# Revit family: Door-Exterior-Simpson-Nantucket-Full_Panel-Single
name_source: partatom
category: Doors
revit_build: Autodesk Revit Architecture 2012 (Build: 20110916_2132(x64)
units: mm (PartAtom-declared; Revit-internal decimal feet)

## types (84) — shared parameters
Assembly Code = B2030230
Bottom Panel Height = 2' - 0 1/8"
Bottom Rail Height = 0' - 8 11/16"
Construction Type = Wood
Description = Nantucket Exterior Door
Frame = Wood - Simpson Doors - Douglas Fir
Frame Projection Ext. = 0' - 1"
Frame Projection Int. = 0' - 1"
Frame Type = Frame : Standard
Frame Width = 0' - 3"
Function = Exterior
Glass Options = http://simpsondoor.com
Innerbond Double Hip-Raised Panel = No
Innerbond Double Hip-Raised Panel Top = No
Manufacturer = Simpsons Door Company
Middle Rail Height 1 = 0' - 3 1/2"
Middle Rail Height 2 = 0' - 6 1/2"
Muntin Width = 0' - 0 3/8"
Number of Panel Dividers = 1
Ovolo Construction = Yes
Panel = Wood - Simpson Doors - Douglas Fir
Panel Divider Width = 0' - 3 1/2"
Panel Stile Width = 0' - 5"
Product Documentation Link = http://www.simpsondoor.com
Product Page URL = http://www.simpsondoor.com
Thickness = 0' - 1 3/4"
Thickness Note = comes in 1 3/4" and 2 1/4" Thickness. Default is set to 1 3/4"
Top Rail Height = 0' - 4 15/16"
URL = http://www.simpsondoor.com
Wall Closure = By host
Wood Species = http://simpsondoor.com

## per-type parameters (varying)
| type | Height | Model | Rough Height | Rough Width | Top Panel | Top Panel Height | Upper Mid Rail | Width |
| 77130 Nantucket 30x80 Ovolo Flat Panel | 6' - 8" | 77130 | 6' - 10" | 2' - 10" | Wood - Simpson Doors - Douglas Fir | 0' - 8 1/8" | Yes | 2' - 6" |
| 77130 Nantucket 30x84 Ovolo Flat Panel | 7' - 0" | 77130 | 7' - 2" | 2' - 10" | Wood - Simpson Doors - Douglas Fir | 0' - 8 1/8" | Yes | 2' - 6" |
| 77130 Nantucket 30x96 Ovolo Flat Panel | 8' - 0" | 77130 | 8' - 2" | 2' - 10" | Wood - Simpson Doors - Douglas Fir | 0' - 8 1/8" | Yes | 2' - 6" |
| 77130 Nantucket 32x80 Ovolo Flat Panel | 6' - 8" | 77130 | 6' - 10" | 3' - 0" | Wood - Simpson Doors - Douglas Fir | 0' - 8 1/8" | Yes | 2' - 8" |
| 77130 Nantucket 32x84 Ovolo Flat Panel | 7' - 0" | 77130 | 7' - 2" | 3' - 0" | Wood - Simpson Doors - Douglas Fir | 0' - 8 1/8" | Yes | 2' - 8" |
| 77130 Nantucket 32x96 Ovolo Flat Panel | 8' - 0" | 77130 | 8' - 2" | 3' - 0" | Wood - Simpson Doors - Douglas Fir | 0' - 8 1/8" | Yes | 2' - 8" |
| 77130 Nantucket 34x80 Ovolo Flat Panel | 6' - 8" | 77130 | 6' - 10" | 3' - 2" | Wood - Simpson Doors - Douglas Fir | 0' - 8 1/8" | Yes | 2' - 10" |
| 77130 Nantucket 34x84 Ovolo Flat Panel | 7' - 0" | 77130 | 7' - 2" | 3' - 2" | Wood - Simpson Doors - Douglas Fir | 0' - 8 1/8" | Yes | 2' - 10" |
| 77130 Nantucket 34x96 Ovolo Flat Panel | 8' - 0" | 77130 | 8' - 2" | 3' - 2" | Wood - Simpson Doors - Douglas Fir | 0' - 8 1/8" | Yes | 2' - 10" |
| 77130 Nantucket 36x80 Ovolo Flat Panel | 6' - 8" | 77130 | 6' - 10" | 3' - 4" | Wood - Simpson Doors - Douglas Fir | 0' - 8 1/8" | Yes | 3' - 0" |
| 77130 Nantucket 36x84 Ovolo Flat Panel | 7' - 0" | 77130 | 7' - 2" | 3' - 4" | Wood - Simpson Doors - Douglas Fir | 0' - 8 1/8" | Yes | 3' - 0" |
| 77130 Nantucket 36x96 Ovolo Flat Panel | 8' - 0" | 77130 | 8' - 2" | 3' - 4" | Wood - Simpson Doors - Douglas Fir | 0' - 8 1/8" | Yes | 3' - 0" |
| 77130 Nantucket 38x80 Ovolo Flat Panel | 6' - 8" | 77130 | 6' - 10" | 3' - 6" | Wood - Simpson Doors - Douglas Fir | 0' - 8 1/8" | Yes | 3' - 2" |
| 77130 Nantucket 38x84 Ovolo Flat Panel | 7' - 0" | 77130 | 7' - 2" | 3' - 6" | Wood - Simpson Doors - Douglas Fir | 0' - 8 1/8" | Yes | 3' - 2" |
| 77130 Nantucket 38x96 Ovolo Flat Panel | 8' - 0" | 77130 | 8' - 2" | 3' - 6" | Wood - Simpson Doors - Douglas Fir | 0' - 8 1/8" | Yes | 3' - 2" |
| 77130 Nantucket 40x80 Ovolo Flat Panel | 6' - 8" | 77130 | 6' - 10" | 3' - 8" | Wood - Simpson Doors - Douglas Fir | 0' - 8 1/8" | Yes | 3' - 4" |
| 77130 Nantucket 40x84 Ovolo Flat Panel | 7' - 0" | 77130 | 7' - 2" | 3' - 8" | Wood - Simpson Doors - Douglas Fir | 0' - 8 1/8" | Yes | 3' - 4" |
| 77130 Nantucket 40x96 Ovolo Flat Panel | 8' - 0" | 77130 | 8' - 2" | 3' - 8" | Wood - Simpson Doors - Douglas Fir | 0' - 8 1/8" | Yes | 3' - 4" |
| 77130 Nantucket 42x80 Ovolo Flat Panel | 6' - 8" | 77130 | 6' - 10" | 3' - 10" | Wood - Simpson Doors - Douglas Fir | 0' - 8 1/8" | Yes | 3' - 6" |
| 77130 Nantucket 42x84 Ovolo Flat Panel | 7' - 0" | 77130 | 7' - 2" | 3' - 10" | Wood - Simpson Doors - Douglas Fir | 0' - 8 1/8" | Yes | 3' - 6" |
| 77130 Nantucket 42x96 Ovolo Flat Panel | 8' - 0" | 77130 | 8' - 2" | 3' - 10" | Wood - Simpson Doors - Douglas Fir | 0' - 8 1/8" | Yes | 3' - 6" |
| 77132 Nantucket 30x80 Ovolo Flat Panel | 6' - 8" | 77132 | 6' - 10" | 2' - 10" | Glass - Simpson Doors - Clear | 0' - 8 1/8" | Yes | 2' - 6" |
| 77132 Nantucket 30x84 Ovolo Flat Panel | 7' - 0" | 77132 | 7' - 2" | 2' - 10" | Glass - Simpson Doors - Clear | 0' - 8 1/8" | Yes | 2' - 6" |
| 77132 Nantucket 30x96 Ovolo Flat Panel | 8' - 0" | 77132 | 8' - 2" | 2' - 10" | Glass - Simpson Doors - Clear | 0' - 8 1/8" | Yes | 2' - 6" |
| 77132 Nantucket 32x80 Ovolo Flat Panel | 6' - 8" | 77132 | 6' - 10" | 3' - 0" | Glass - Simpson Doors - Clear | 0' - 8 1/8" | Yes | 2' - 8" |
| 77132 Nantucket 32x84 Ovolo Flat Panel | 7' - 0" | 77132 | 7' - 2" | 3' - 0" | Glass - Simpson Doors - Clear | 0' - 8 1/8" | Yes | 2' - 8" |
| 77132 Nantucket 32x96 Ovolo Flat Panel | 8' - 0" | 77132 | 8' - 2" | 3' - 0" | Glass - Simpson Doors - Clear | 0' - 8 1/8" | Yes | 2' - 8" |
| 77132 Nantucket 34x80 Ovolo Flat Panel | 6' - 8" | 77132 | 6' - 10" | 3' - 2" | Glass - Simpson Doors - Clear | 0' - 8 1/8" | Yes | 2' - 10" |
| 77132 Nantucket 34x84 Ovolo Flat Panel | 7' - 0" | 77132 | 7' - 2" | 3' - 2" | Glass - Simpson Doors - Clear | 0' - 8 1/8" | Yes | 2' - 10" |
| 77132 Nantucket 34x96 Ovolo Flat Panel | 8' - 0" | 77132 | 8' - 2" | 3' - 2" | Glass - Simpson Doors - Clear | 0' - 8 1/8" | Yes | 2' - 10" |
| 77132 Nantucket 36x80 Ovolo Flat Panel | 6' - 8" | 77132 | 6' - 10" | 3' - 4" | Glass - Simpson Doors - Clear | 0' - 8 1/8" | Yes | 3' - 0" |
| 77132 Nantucket 36x84 Ovolo Flat Panel | 7' - 0" | 77132 | 7' - 2" | 3' - 4" | Glass - Simpson Doors - Clear | 0' - 8 1/8" | Yes | 3' - 0" |
| 77132 Nantucket 36x96 Ovolo Flat Panel | 8' - 0" | 77132 | 8' - 2" | 3' - 4" | Glass - Simpson Doors - Clear | 0' - 8 1/8" | Yes | 3' - 0" |
| 77132 Nantucket 38x80 Ovolo Flat Panel | 6' - 8" | 77132 | 6' - 10" | 3' - 6" | Glass - Simpson Doors - Clear | 0' - 8 1/8" | Yes | 3' - 2" |
| 77132 Nantucket 38x84 Ovolo Flat Panel | 7' - 0" | 77132 | 7' - 2" | 3' - 6" | Glass - Simpson Doors - Clear | 0' - 8 1/8" | Yes | 3' - 2" |
| 77132 Nantucket 38x96 Ovolo Flat Panel | 8' - 0" | 77132 | 8' - 2" | 3' - 6" | Glass - Simpson Doors - Clear | 0' - 8 1/8" | Yes | 3' - 2" |
| 77132 Nantucket 40x80 Ovolo Flat Panel | 6' - 8" | 77132 | 6' - 10" | 3' - 8" | Glass - Simpson Doors - Clear | 0' - 8 1/8" | Yes | 3' - 4" |
| 77132 Nantucket 40x84 Ovolo Flat Panel | 7' - 0" | 77132 | 7' - 2" | 3' - 8" | Glass - Simpson Doors - Clear | 0' - 8 1/8" | Yes | 3' - 4" |
| 77132 Nantucket 40x96 Ovolo Flat Panel | 8' - 0" | 77132 | 8' - 2" | 3' - 8" | Glass - Simpson Doors - Clear | 0' - 8 1/8" | Yes | 3' - 4" |
| 77132 Nantucket 42x80 Ovolo Flat Panel | 6' - 8" | 77132 | 6' - 10" | 3' - 10" | Glass - Simpson Doors - Clear | 0' - 8 1/8" | Yes | 3' - 6" |
| 77132 Nantucket 42x84 Ovolo Flat Panel | 7' - 0" | 77132 | 7' - 2" | 3' - 10" | Glass - Simpson Doors - Clear | 0' - 8 1/8" | Yes | 3' - 6" |
| 77132 Nantucket 42x96 Ovolo Flat Panel | 8' - 0" | 77132 | 8' - 2" | 3' - 10" | Glass - Simpson Doors - Clear | 0' - 8 1/8" | Yes | 3' - 6" |
| 77144 Nantucket 30x80 Ovolo Flat Panel | 6' - 8" | 77144 | 6' - 10" | 2' - 10" | Wood - Simpson Doors - Douglas Fir | 0' - 8 1/8" | No | 2' - 6" |
| 77144 Nantucket 30x84 Ovolo Flat Panel | 7' - 0" | 77144 | 7' - 2" | 2' - 10" | Wood - Simpson Doors - Douglas Fir | 0' - 8 1/8" | No | 2' - 6" |
| 77144 Nantucket 30x96 Ovolo Flat Panel | 8' - 0" | 77144 | 8' - 2" | 2' - 10" | Wood - Simpson Doors - Douglas Fir | 0' - 8 1/8" | No | 2' - 6" |
| 77144 Nantucket 32x80 Ovolo Flat Panel | 6' - 8" | 77144 | 6' - 10" | 3' - 0" | Wood - Simpson Doors - Douglas Fir | 0' - 8 1/8" | No | 2' - 8" |
| 77144 Nantucket 32x84 Ovolo Flat Panel | 7' - 0" | 77144 | 7' - 2" | 3' - 0" | Wood - Simpson Doors - Douglas Fir | 0' - 8 1/8" | No | 2' - 8" |
| 77144 Nantucket 32x96 Ovolo Flat Panel | 8' - 0" | 77144 | 8' - 2" | 3' - 0" | Wood - Simpson Doors - Douglas Fir | 0' - 8 1/8" | No | 2' - 8" |
| 77144 Nantucket 34x80 Ovolo Flat Panel | 6' - 8" | 77144 | 6' - 10" | 3' - 2" | Wood - Simpson Doors - Douglas Fir | 0' - 8 1/8" | No | 2' - 10" |
| 77144 Nantucket 34x84 Ovolo Flat Panel | 7' - 0" | 77144 | 7' - 2" | 3' - 2" | Wood - Simpson Doors - Douglas Fir | 0' - 8 1/8" | No | 2' - 10" |
| 77144 Nantucket 34x96 Ovolo Flat Panel | 8' - 0" | 77144 | 8' - 2" | 3' - 2" | Wood - Simpson Doors - Douglas Fir | 0' - 8 1/8" | No | 2' - 10" |
| 77144 Nantucket 36x80 Ovolo Flat Panel | 6' - 8" | 77144 | 6' - 10" | 3' - 4" | Wood - Simpson Doors - Douglas Fir | 0' - 8 1/8" | No | 3' - 0" |
| 77144 Nantucket 36x84 Ovolo Flat Panel | 7' - 0" | 77144 | 7' - 2" | 3' - 4" | Wood - Simpson Doors - Douglas Fir | 0' - 8 1/8" | No | 3' - 0" |
| 77144 Nantucket 36x96 Ovolo Flat Panel | 8' - 0" | 77144 | 8' - 2" | 3' - 4" | Wood - Simpson Doors - Douglas Fir | 0' - 8 1/8" | No | 3' - 0" |
| 77144 Nantucket 38x80 Ovolo Flat Panel | 6' - 8" | 77144 | 6' - 10" | 3' - 6" | Wood - Simpson Doors - Douglas Fir | 0' - 8 1/8" | No | 3' - 2" |
| 77144 Nantucket 38x84 Ovolo Flat Panel | 7' - 0" | 77144 | 7' - 2" | 3' - 6" | Wood - Simpson Doors - Douglas Fir | 0' - 8 1/8" | No | 3' - 2" |
| 77144 Nantucket 38x96 Ovolo Flat Panel | 8' - 0" | 77144 | 8' - 2" | 3' - 6" | Wood - Simpson Doors - Douglas Fir | 0' - 8 1/8" | No | 3' - 2" |
| 77144 Nantucket 40x80 Ovolo Flat Panel | 6' - 8" | 77144 | 6' - 10" | 3' - 8" | Wood - Simpson Doors - Douglas Fir | 0' - 8 1/8" | No | 3' - 4" |
| 77144 Nantucket 40x84 Ovolo Flat Panel | 7' - 0" | 77144 | 7' - 2" | 3' - 8" | Wood - Simpson Doors - Douglas Fir | 0' - 8 1/8" | No | 3' - 4" |
| 77144 Nantucket 40x96 Ovolo Flat Panel | 8' - 0" | 77144 | 8' - 2" | 3' - 8" | Wood - Simpson Doors - Douglas Fir | 0' - 8 1/8" | No | 3' - 4" |
| 77144 Nantucket 42x80 Ovolo Flat Panel | 6' - 8" | 77144 | 6' - 10" | 3' - 10" | Wood - Simpson Doors - Douglas Fir | 0' - 8 1/8" | No | 3' - 6" |
| 77144 Nantucket 42x84 Ovolo Flat Panel | 7' - 0" | 77144 | 7' - 2" | 3' - 10" | Wood - Simpson Doors - Douglas Fir | 0' - 8 1/8" | No | 3' - 6" |
| 77144 Nantucket 42x96 Ovolo Flat Panel | 8' - 0" | 77144 | 8' - 2" | 3' - 10" | Wood - Simpson Doors - Douglas Fir | 0' - 8 1/8" | No | 3' - 6" |
| 77167 Nantucket 30x80 Ovolo Flat Panel | 6' - 8" | 77167 | 6' - 10" | 2' - 10" | Wood - Simpson Doors - Douglas Fir | 2' - 0 1/8" | Yes | 2' - 6" |
| 77167 Nantucket 30x84 Ovolo Flat Panel | 7' - 0" | 77167 | 7' - 2" | 2' - 10" | Wood - Simpson Doors - Douglas Fir | 2' - 4 1/8" | Yes | 2' - 6" |
| 77167 Nantucket 30x96 Ovolo Flat Panel | 8' - 0" | 77167 | 8' - 2" | 2' - 10" | Wood - Simpson Doors - Douglas Fir | 3' - 4 1/8" | Yes | 2' - 6" |
| 77167 Nantucket 32x80 Ovolo Flat Panel | 6' - 8" | 77167 | 6' - 10" | 3' - 0" | Wood - Simpson Doors - Douglas Fir | 2' - 0 1/8" | Yes | 2' - 8" |
| 77167 Nantucket 32x84 Ovolo Flat Panel | 7' - 0" | 77167 | 7' - 2" | 3' - 0" | Wood - Simpson Doors - Douglas Fir | 2' - 4 1/8" | Yes | 2' - 8" |
| 77167 Nantucket 32x96 Ovolo Flat Panel | 8' - 0" | 77167 | 8' - 2" | 3' - 0" | Wood - Simpson Doors - Douglas Fir | 3' - 4 1/8" | Yes | 2' - 8" |
| 77167 Nantucket 34x80 Ovolo Flat Panel | 6' - 8" | 77167 | 6' - 10" | 3' - 2" | Wood - Simpson Doors - Douglas Fir | 2' - 0 1/8" | Yes | 2' - 10" |
| 77167 Nantucket 34x84 Ovolo Flat Panel | 7' - 0" | 77167 | 7' - 2" | 3' - 2" | Wood - Simpson Doors - Douglas Fir | 2' - 4 1/8" | Yes | 2' - 10" |
| 77167 Nantucket 34x96 Ovolo Flat Panel | 8' - 0" | 77167 | 8' - 2" | 3' - 2" | Wood - Simpson Doors - Douglas Fir | 3' - 4 1/8" | Yes | 2' - 10" |
| 77167 Nantucket 36x80 Ovolo Flat Panel | 6' - 8" | 77167 | 6' - 10" | 3' - 4" | Wood - Simpson Doors - Douglas Fir | 2' - 0 1/8" | Yes | 3' - 0" |
| 77167 Nantucket 36x84 Ovolo Flat Panel | 7' - 0" | 77167 | 7' - 2" | 3' - 4" | Wood - Simpson Doors - Douglas Fir | 2' - 4 1/8" | Yes | 3' - 0" |
| 77167 Nantucket 36x96 Ovolo Flat Panel | 8' - 0" | 77167 | 8' - 2" | 3' - 4" | Wood - Simpson Doors - Douglas Fir | 3' - 4 1/8" | Yes | 3' - 0" |
| 77167 Nantucket 38x80 Ovolo Flat Panel | 6' - 8" | 77167 | 6' - 10" | 3' - 6" | Wood - Simpson Doors - Douglas Fir | 2' - 0 1/8" | Yes | 3' - 2" |
| 77167 Nantucket 38x84 Ovolo Flat Panel | 7' - 0" | 77167 | 7' - 2" | 3' - 6" | Wood - Simpson Doors - Douglas Fir | 2' - 4 1/8" | Yes | 3' - 2" |
| 77167 Nantucket 38x96 Ovolo Flat Panel | 8' - 0" | 77167 | 8' - 2" | 3' - 6" | Wood - Simpson Doors - Douglas Fir | 3' - 4 1/8" | Yes | 3' - 2" |
| 77167 Nantucket 40x80 Ovolo Flat Panel | 6' - 8" | 77167 | 6' - 10" | 3' - 8" | Wood - Simpson Doors - Douglas Fir | 2' - 0 1/8" | Yes | 3' - 4" |
| 77167 Nantucket 40x84 Ovolo Flat Panel | 7' - 0" | 77167 | 7' - 2" | 3' - 8" | Wood - Simpson Doors - Douglas Fir | 2' - 4 1/8" | Yes | 3' - 4" |
| 77167 Nantucket 40x96 Ovolo Flat Panel | 8' - 0" | 77167 | 8' - 2" | 3' - 8" | Wood - Simpson Doors - Douglas Fir | 3' - 4 1/8" | Yes | 3' - 4" |
| 77167 Nantucket 42x80 Ovolo Flat Panel | 6' - 8" | 77167 | 6' - 10" | 3' - 10" | Wood - Simpson Doors - Douglas Fir | 2' - 0 1/8" | Yes | 3' - 6" |
| 77167 Nantucket 42x84 Ovolo Flat Panel | 7' - 0" | 77167 | 7' - 2" | 3' - 10" | Wood - Simpson Doors - Douglas Fir | 2' - 4 1/8" | Yes | 3' - 6" |
| 77167 Nantucket 42x96 Ovolo Flat Panel | 8' - 0" | 77167 | 8' - 2" | 3' - 10" | Wood - Simpson Doors - Douglas Fir | 3' - 4 1/8" | Yes | 3' - 6" |

## geometry (parser evidence)
native form markers: Blend x6, Sweep x20
no freeform markers — native parametric forms only
